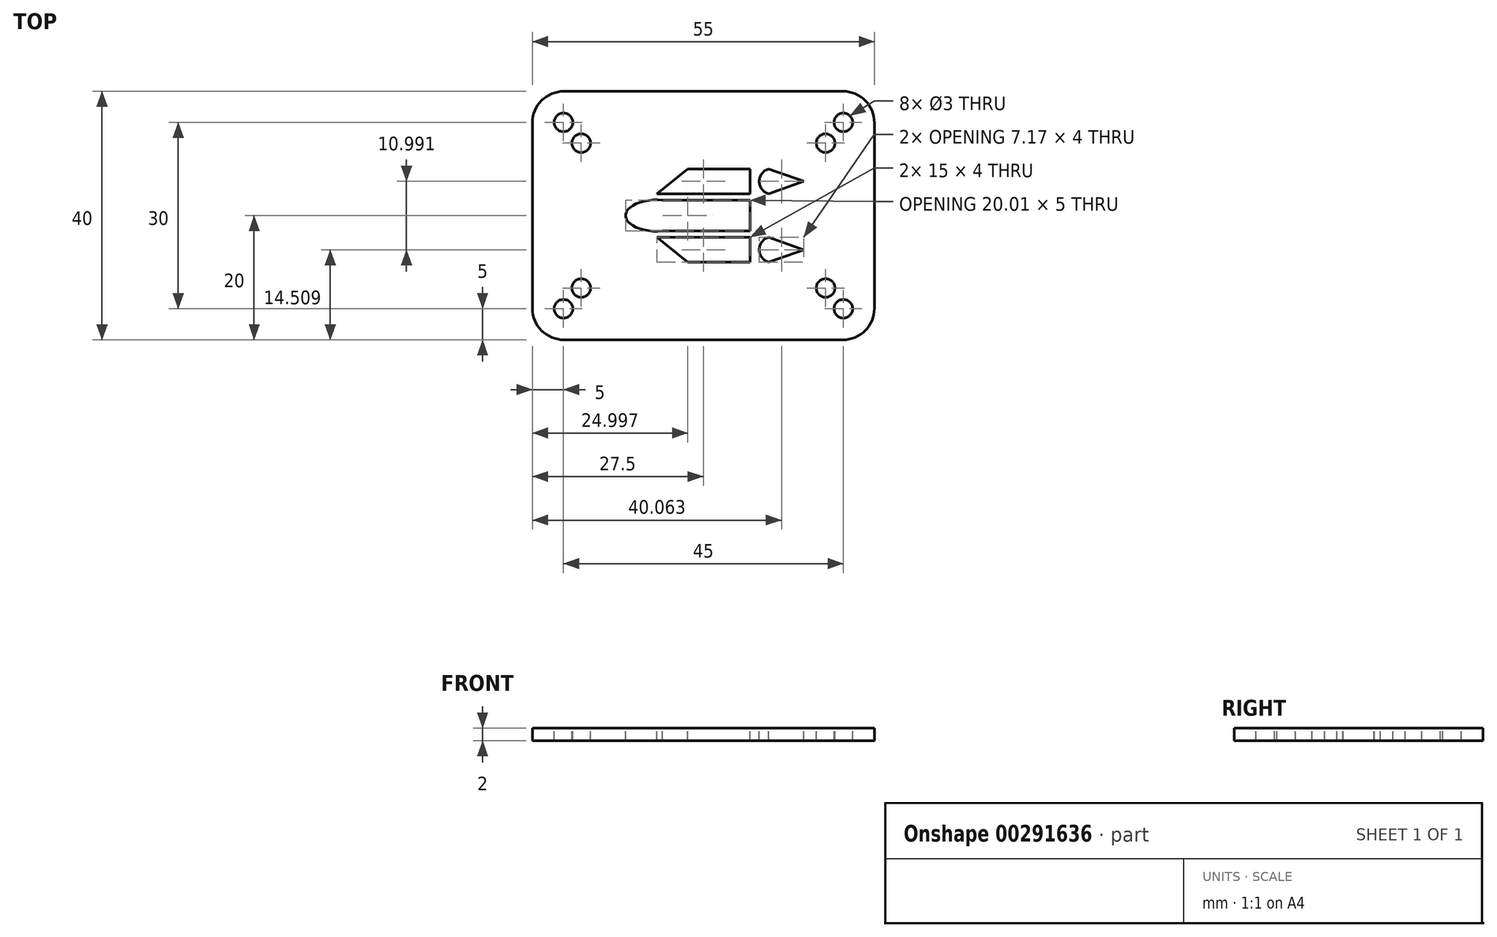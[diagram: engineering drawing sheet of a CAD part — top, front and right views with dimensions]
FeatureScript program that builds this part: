
annotation { "Feature Type Name" : "Feature", "Feature Type Description" : "" }
export const myFeature = defineFeature(function(context is Context, id is Id, definition is map)
    precondition{}
    {
        {
            var Q0;
            Q0=qCreatedBy(makeId("Top.planeOp"),FACE);
            var sketch = newSketch(context, id + "F0", { "sketchPlane" : qUnion([Q0])});
            skLineSegment(sketch, "E0.bottom", {"start": v(0, 0) * mm, "end": v(55, 0) * mm});
            skLineSegment(sketch, "E0.top", {"start": v(0, 40) * mm, "end": v(55, 40) * mm});
            skLineSegment(sketch, "E0.left", {"start": v(0, 0) * mm, "end": v(0, 40) * mm});
            skLineSegment(sketch, "E0.right", {"start": v(55, 0) * mm, "end": v(55, 40) * mm});
            skSolve(sketch);
        }
        {
            var Q0;
            Q0=qSketchRegion(id+"F0",true);
            extrude(context, id + "F1", {"entities" : qUnion([Q0]), "depth" : 2 * mm});
        }
        {
            var Q0;
            Q0=makeQuery(id+"F1.opExtrude","CAP_FACE",FACE,{"disambiguationData":[OSD([sQuery(id+"F0.wireOp",EDGE,"E0.bottom"),sQuery(id+"F0.wireOp",EDGE,"E0.top"),sQuery(id+"F0.wireOp",EDGE,"E0.left"),sQuery(id+"F0.wireOp",EDGE,"E0.right")])],"isStart":false});
            cPlane(context, id + "F2", {"entities" : qUnion([Q0]), "cplaneType" : CPlaneType.OFFSET, "offset" : 0 * mm, "width" : 152.4 * mm, "height" : 152.4 * mm});
        }
        {
            var Q0;
            Q0=makeQuery(id+"F1.opExtrude","SWEPT_EDGE",EDGE,{"disambiguationData":[OSD([sQuery(id+"F0.wireOp",EDGE,"E0.bottom"),sQuery(id+"F0.wireOp",EDGE,"E0.right")])]});
            fillet(context, id + "F3", {"entities" : qUnion([Q0]), "radius" : 5.08 * mm, "tangentPropagation" : true, "allowEdgeOverflow" : false});
        }
        {
            var Q0;
            Q0=makeQuery(id+"F1.opExtrude","SWEPT_EDGE",EDGE,{"disambiguationData":[OSD([sQuery(id+"F0.wireOp",EDGE,"E0.top"),sQuery(id+"F0.wireOp",EDGE,"E0.right")])]});
            fillet(context, id + "F4", {"entities" : qUnion([Q0]), "radius" : 5.08 * mm, "tangentPropagation" : true, "allowEdgeOverflow" : false});
        }
        {
            var Q0;
            Q0=makeQuery(id+"F1.opExtrude","SWEPT_EDGE",EDGE,{"disambiguationData":[OSD([sQuery(id+"F0.wireOp",EDGE,"E0.top"),sQuery(id+"F0.wireOp",EDGE,"E0.left")])]});
            fillet(context, id + "F5", {"entities" : qUnion([Q0]), "radius" : 5.08 * mm, "tangentPropagation" : true, "allowEdgeOverflow" : false});
        }
        {
            var Q0;
            Q0=makeQuery(id+"F1.opExtrude","SWEPT_EDGE",EDGE,{"disambiguationData":[OSD([sQuery(id+"F0.wireOp",EDGE,"E0.bottom"),sQuery(id+"F0.wireOp",EDGE,"E0.left")])]});
            fillet(context, id + "F6", {"entities" : qUnion([Q0]), "radius" : 5.08 * mm, "tangentPropagation" : true, "allowEdgeOverflow" : false});
        }
        {
            var Q0;
            Q0=qCreatedBy(id+"F2.planeOp",FACE);
            var sketch = newSketch(context, id + "F7", { "sketchPlane" : qUnion([Q0])});
            skLineSegment(sketch, "E1", {"start": v(27.5, 0) * mm, "end": v(27.5, 70.78) * mm});
            skLineSegment(sketch, "E2", {"start": v(0, 20) * mm, "end": v(105.16, 20) * mm});
            skSolve(sketch);
        }
        {
            var Q0;
            Q0=qCreatedBy(id+"F2.planeOp",FACE);
            var sketch = newSketch(context, id + "F8", { "sketchPlane" : qUnion([Q0])});
            skCircle(sketch, "E3", {"center": v(50, 5) * mm, "radius": 1.5 * mm});
            skCircle(sketch, "E4", {"center": v(47.15, 8.34) * mm, "radius": 1.5 * mm});
            skCircle(sketch, "E5.MirrorC", {"center": v(47.15, 31.66) * mm, "radius": 1.5 * mm});
            skCircle(sketch, "E6.MirrorC", {"center": v(50, 35) * mm, "radius": 1.5 * mm});
            skCircle(sketch, "E7.MirrorC", {"center": v(7.85, 31.66) * mm, "radius": 1.5 * mm});
            skCircle(sketch, "E8.MirrorC", {"center": v(5, 35) * mm, "radius": 1.5 * mm});
            skCircle(sketch, "E9.MirrorC", {"center": v(7.85, 8.34) * mm, "radius": 1.5 * mm});
            skCircle(sketch, "E10.MirrorC", {"center": v(5, 5) * mm, "radius": 1.5 * mm});
            skSolve(sketch);
        }
        {
            var Q0;
            Q0=qSketchRegion(id+"F8",true);
            extrude(context, id + "F9", {"entities" : qUnion([Q0]), "operationType" : NewBodyOperationType.REMOVE, "oppositeDirection" : true, "depth" : 25.4 * mm});
        }
        {
            var Q0;
            Q0=makeQuery(id+"F1.opExtrude","CAP_FACE",FACE,{"disambiguationData":[OSD([sQuery(id+"F0.wireOp",EDGE,"E0.bottom"),sQuery(id+"F0.wireOp",EDGE,"E0.top"),sQuery(id+"F0.wireOp",EDGE,"E0.left"),sQuery(id+"F0.wireOp",EDGE,"E0.right")])],"isStart":false});
            var sketch = newSketch(context, id + "F10", { "sketchPlane" : qUnion([Q0])});
            skLineSegment(sketch, "E11.bottom", {"start": v(20, 22.5) * mm, "end": v(35, 22.5) * mm});
            skLineSegment(sketch, "E11.top", {"start": v(20, 17.5) * mm, "end": v(35, 17.5) * mm});
            skLineSegment(sketch, "E11.left", {"start": v(20, 22.5) * mm, "end": v(20, 17.5) * mm});
            skLineSegment(sketch, "E11.right", {"start": v(35, 22.5) * mm, "end": v(35, 17.5) * mm});
            skEllipse(sketch, "E12", {"center": v(20, 20) * mm, "majorRadius": 5 * mm, "minorRadius": 2.54 * mm, "majorAxis": v(-1, 0)});
            skLineSegment(sketch, "E13.bottom", {"start": v(25, 27.5) * mm, "end": v(35, 27.5) * mm});
            skLineSegment(sketch, "E13.top", {"start": v(25, 23.5) * mm, "end": v(35, 23.5) * mm});
            skLineSegment(sketch, "E13.left", {"start": v(25, 27.5) * mm, "end": v(25, 23.5) * mm});
            skLineSegment(sketch, "E13.right", {"start": v(35, 27.5) * mm, "end": v(35, 23.5) * mm});
            skLineSegment(sketch, "E14", {"start": v(25, 27.5) * mm, "end": v(20, 23.5) * mm});
            skLineSegment(sketch, "E15", {"start": v(20, 23.5) * mm, "end": v(25, 23.5) * mm});
            skLineSegment(sketch, "E16.MirrorCS", {"start": v(25, 12.5) * mm, "end": v(20, 16.5) * mm});
            skLineSegment(sketch, "E17.MirrorCS", {"start": v(16.95, 16.5) * mm, "end": v(25, 16.5) * mm});
            skLineSegment(sketch, "E18.MirrorCS", {"start": v(25, 12.5) * mm, "end": v(25, 16.5) * mm});
            skLineSegment(sketch, "E19.MirrorCS", {"start": v(25, 16.5) * mm, "end": v(35, 16.5) * mm});
            skLineSegment(sketch, "E20.MirrorCS", {"start": v(21.95, 12.5) * mm, "end": v(35, 12.5) * mm});
            skLineSegment(sketch, "E21.MirrorCS", {"start": v(35, 12.5) * mm, "end": v(35, 16.5) * mm});
            skArc(sketch, "E22", {"start": v(38, 27.5) * mm, "mid": v(36.48, 25.5) * mm, "end": v(38, 23.5) * mm});
            skArc(sketch, "E23.MirrorCS", {"start": v(38, 12.5) * mm, "mid": v(36.48, 14.5) * mm, "end": v(38, 16.5) * mm});
            skLineSegment(sketch, "E24", {"start": v(38, 27.5) * mm, "end": v(43.65, 25.5) * mm});
            skLineSegment(sketch, "E25", {"start": v(43.65, 25.5) * mm, "end": v(38, 23.5) * mm});
            skLineSegment(sketch, "E26.MirrorCS", {"start": v(43.65, 14.5) * mm, "end": v(38, 16.5) * mm});
            skLineSegment(sketch, "E27.MirrorCS", {"start": v(38, 12.5) * mm, "end": v(43.65, 14.5) * mm});
            skSolve(sketch);
        }
        {
            var Q0;
            Q0 = qSketchRegion(id + "F10", true);
            extrude(context, id + "F11", {"entities" : qUnion([Q0]), "operationType" : NewBodyOperationType.REMOVE, "oppositeDirection" : true, "depth" : 25.4 * mm, "offsetDistance" : 25.4 * mm});
        }
    });
